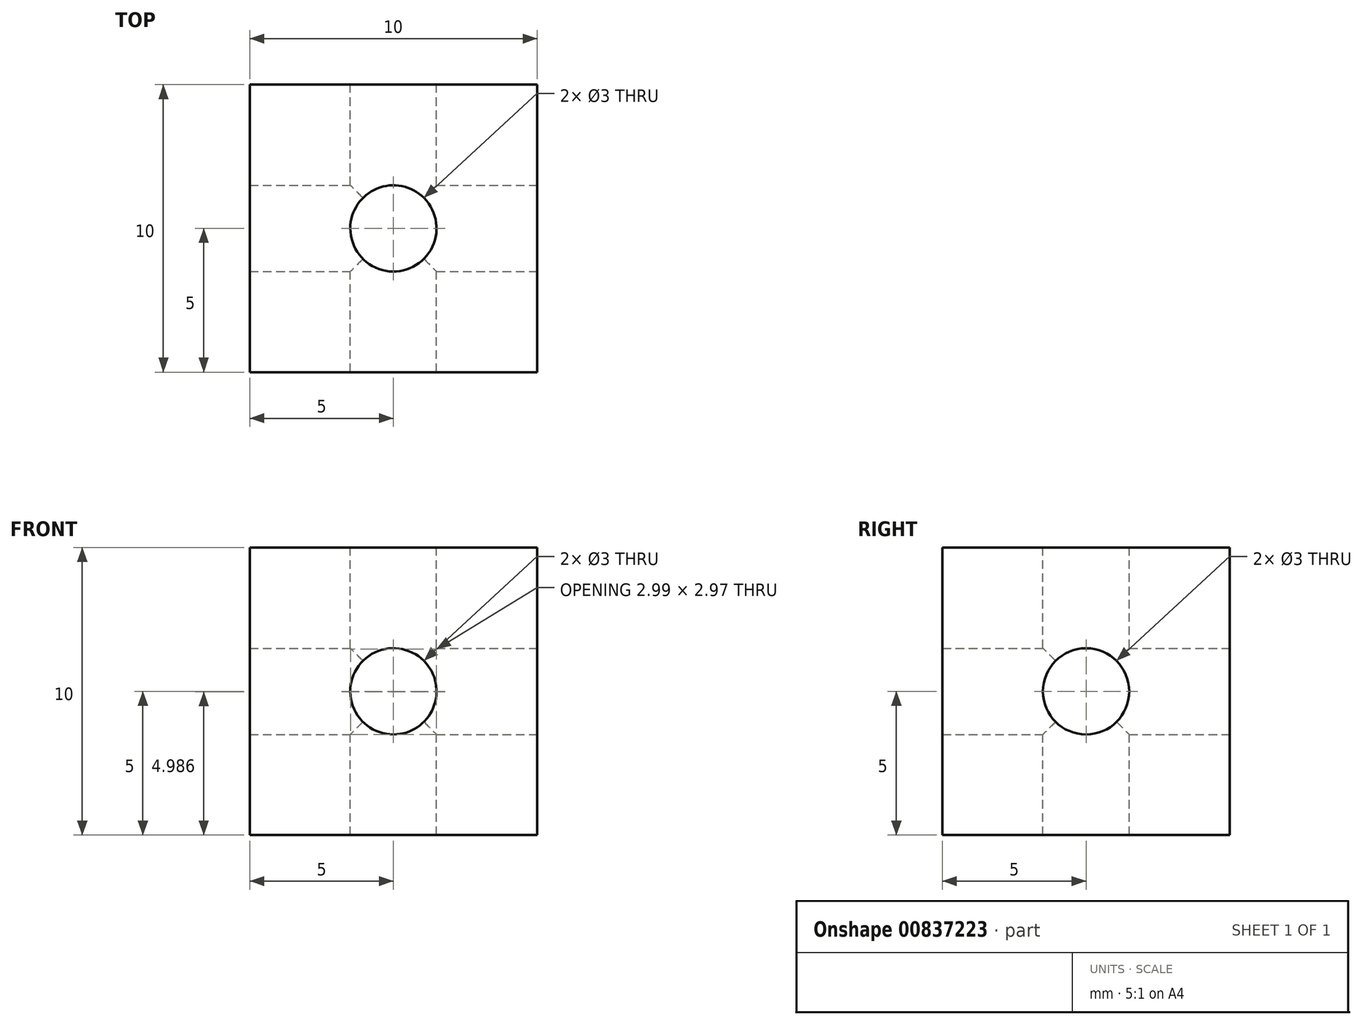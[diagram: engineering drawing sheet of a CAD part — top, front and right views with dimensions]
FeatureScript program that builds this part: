
annotation { "Feature Type Name" : "Feature", "Feature Type Description" : "" }
export const myFeature = defineFeature(function(context is Context, id is Id, definition is map)
    precondition{}
    {
        {
            var Q0;
            Q0=qCreatedBy(makeId("Front.planeOp"),FACE);
            var sketch = newSketch(context, id + "F0", { "sketchPlane" : qUnion([Q0])});
            skLineSegment(sketch, "E0.bottom", {"start": v(5, 5) * mm, "end": v(-5, 5) * mm});
            skLineSegment(sketch, "E0.top", {"start": v(5, -5) * mm, "end": v(-5, -5) * mm});
            skLineSegment(sketch, "E0.left", {"start": v(5, 5) * mm, "end": v(5, -5) * mm});
            skLineSegment(sketch, "E0.right", {"start": v(-5, 5) * mm, "end": v(-5, -5) * mm});
            skPoint(sketch, "E0.middle", {"position": v(0, 0) * mm});
            skCircle(sketch, "E1", {"center": v(0, 0) * mm, "radius": 1.5 * mm});
            skSolve(sketch);
        }
        {
            var Q0;
            Q0 = qSketchRegion(id + "F0", true);
            extrude(context, id + "F1", {"entities" : qUnion([Q0]), "depth" : 10 * mm, "offsetDistance" : 25 * mm});
        }
        {
            var Q0;
            Q0=qCreatedBy(makeId("Top.planeOp"),FACE);
            var sketch = newSketch(context, id + "F2", { "sketchPlane" : qUnion([Q0])});
            skCircle(sketch, "E2", {"center": v(0, -5) * mm, "radius": 1.5 * mm});
            skSolve(sketch);
        }
        {
            var Q0;
            Q0 = qSketchRegion(id + "F2", true);
            extrude(context, id + "F3", {"entities" : qUnion([Q0]), "operationType" : NewBodyOperationType.REMOVE, "endBound" : BoundingType.SYMMETRIC, "oppositeDirection" : true, "depth" : 25 * mm, "offsetDistance" : 25 * mm});
        }
        {
            var Q0;
            Q0=qCreatedBy(makeId("Right.planeOp"),FACE);
            var sketch = newSketch(context, id + "F4", { "sketchPlane" : qUnion([Q0])});
            skCircle(sketch, "E3", {"center": v(-5, 0) * mm, "radius": 1.5 * mm});
            skSolve(sketch);
        }
        {
            var Q0;
            Q0=makeQuery(id+"F4.imprint","IMPRINT",FACE,{"disambiguationData":[TD([[makeQuery(id+"F4.imprint","IMPRINT",EDGE,{"derivedFrom":sQuery(id+"F4.wireOp",EDGE,"E3")}),1.0]])]});
            var Q1;
            Q1=sQuery(id+"F4.wireOp",EDGE,"E3");
            extrude(context, id + "F5", {"entities" : qUnion([Q0]), "operationType" : NewBodyOperationType.REMOVE, "surfaceEntities" : qUnion([Q1]), "endBound" : BoundingType.SYMMETRIC, "oppositeDirection" : true, "depth" : 25 * mm, "offsetDistance" : 25 * mm});
        }
    });
